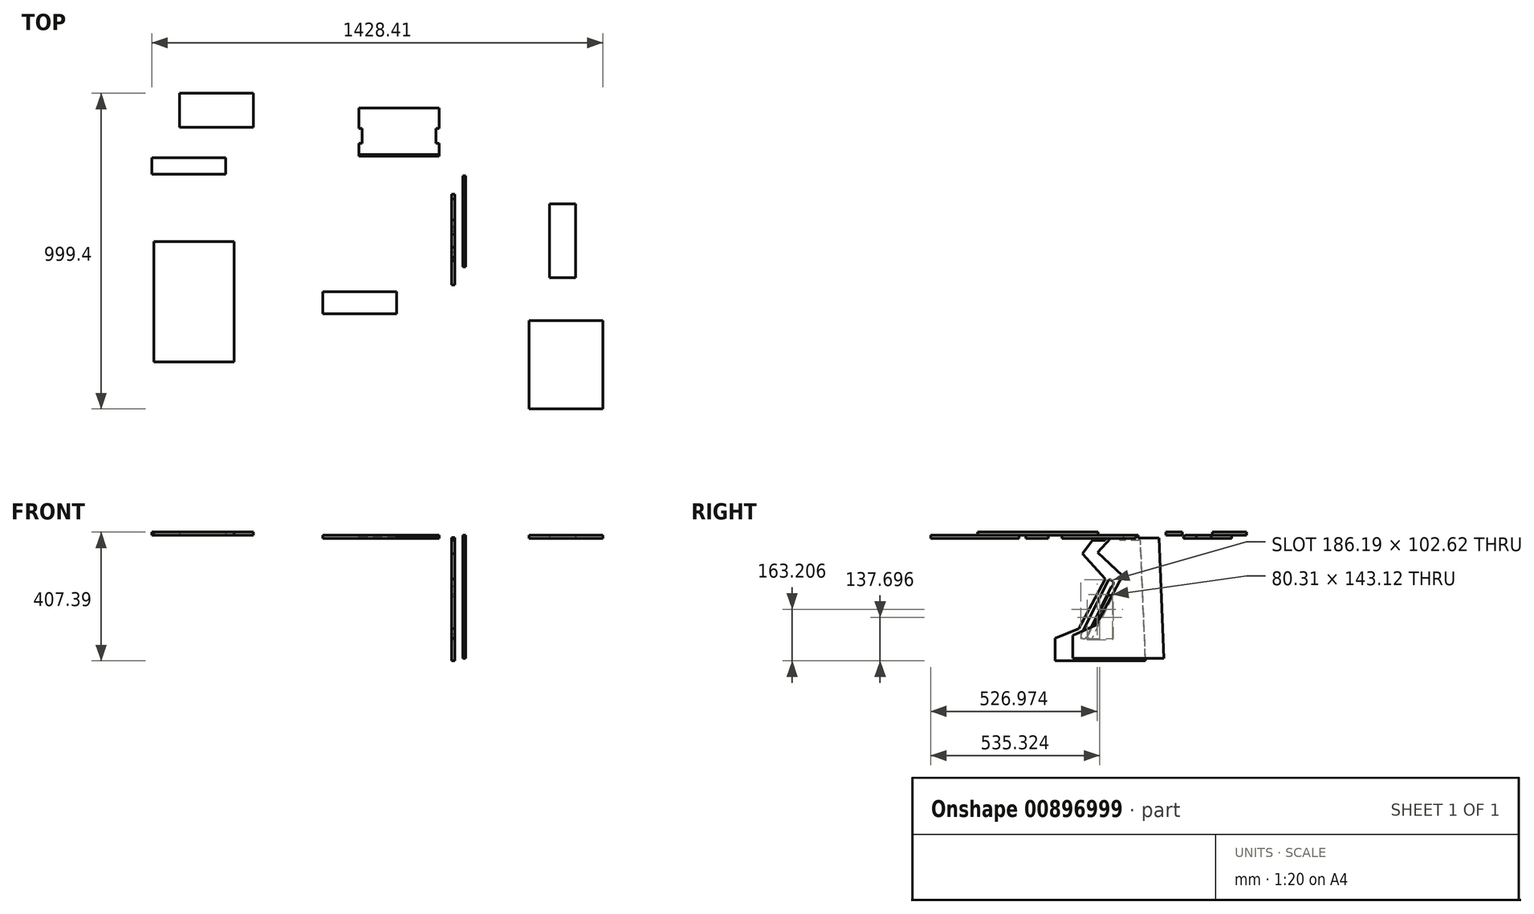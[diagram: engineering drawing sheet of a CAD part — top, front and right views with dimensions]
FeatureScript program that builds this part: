
annotation { "Feature Type Name" : "Feature", "Feature Type Description" : "" }
export const myFeature = defineFeature(function(context is Context, id is Id, definition is map)
    precondition{}
    {
        {
            var Q0;
            Q0=qCreatedBy(makeId("Right.planeOp"),FACE);
            var sketch = newSketch(context, id + "F0", { "sketchPlane" : qUnion([Q0])});
            skLineSegment(sketch, "E0", {"start": v(-57.5, -182.39) * mm, "end": v(221.9, -182.39) * mm});
            skLineSegment(sketch, "E1", {"start": v(221.9, -182.39) * mm, "end": v(205.76, 198.27) * mm});
            skLineSegment(sketch, "E2", {"start": v(94.6, 76.92) * mm, "end": v(10.95, -79.97) * mm});
            skLineSegment(sketch, "E3", {"start": v(-64.8, -182.39) * mm, "end": v(-57.5, -182.39) * mm});
            skLineSegment(sketch, "E4", {"start": v(94.6, 76.92) * mm, "end": v(21.95, 156.83) * mm});
            skLineSegment(sketch, "E5", {"start": v(21.95, 156.83) * mm, "end": v(53.36, 198.27) * mm});
            skLineSegment(sketch, "E6", {"start": v(10.95, -79.97) * mm, "end": v(-64.8, -111.39) * mm});
            skLineSegment(sketch, "E7", {"start": v(-64.8, -111.39) * mm, "end": v(-64.8, -182.39) * mm});
            skArc(sketch, "E8", {"start": v(112.88, 52.28) * mm, "mid": v(119.25, 66.78) * mm, "end": v(104.75, 73.15) * mm});
            skLineSegment(sketch, "E9", {"start": v(112.88, 52.28) * mm, "end": v(34.43, -107.28) * mm});
            skArc(sketch, "E10", {"start": v(18.86, -98.05) * mm, "mid": v(21.66, -111.08) * mm, "end": v(34.43, -107.28) * mm});
            skLineSegment(sketch, "E11", {"start": v(18.86, -98.05) * mm, "end": v(104.75, 73.15) * mm});
            skLineSegment(sketch, "E12", {"start": v(36.9, -108.73) * mm, "end": v(104.01, 26.86) * mm});
            skLineSegment(sketch, "E13", {"start": v(104.01, 26.86) * mm, "end": v(117.2, 20.33) * mm});
            skLineSegment(sketch, "E14", {"start": v(117.2, 20.33) * mm, "end": v(49.6, -116.25) * mm});
            skLineSegment(sketch, "E15", {"start": v(49.6, -116.25) * mm, "end": v(36.9, -108.73) * mm});
            skLineSegment(sketch, "E16", {"start": v(94.36, 198.27) * mm, "end": v(94.36, 207.6) * mm});
            skLineSegment(sketch, "E17", {"start": v(94.36, 207.6) * mm, "end": v(140.76, 207.6) * mm});
            skLineSegment(sketch, "E18", {"start": v(140.76, 207.6) * mm, "end": v(140.76, 198.27) * mm});
            skLineSegment(sketch, "E19", {"start": v(205.76, 198.27) * mm, "end": v(140.76, 198.27) * mm});
            skLineSegment(sketch, "E20", {"start": v(140.76, 198.27) * mm, "end": v(94.36, 198.27) * mm});
            skLineSegment(sketch, "E21", {"start": v(53.36, 198.27) * mm, "end": v(94.36, 198.27) * mm});
            skSolve(sketch);
        }
        {
            var Q0;
            Q0 = qSketchRegion(id + "F0", true);
            extrude(context, id + "F1", {"entities" : qUnion([Q0]), "depth" : 10 * mm, "offsetDistance" : 25 * mm});
        }
        {
            var Q0;
            Q0=makeQuery(id+"F1.opExtrude","CAP_FACE",FACE,{"disambiguationData":[OSD([sQuery(id+"F0.wireOp",EDGE,"E0"),sQuery(id+"F0.wireOp",EDGE,"E1"),sQuery(id+"F0.wireOp",EDGE,"lHdpLVMJ-1WkC-JgKl-GBrL-0Ag0FSk1Ueil"),sQuery(id+"F0.wireOp",EDGE,"8fRossxI-SsTZ-U6cr-KrP5-VSivJObJp7ZS"),sQuery(id+"F0.wireOp",EDGE,"kheAgBa6-kGJ1-7C4r-LUex-SDBD7PTxrj8S"),sQuery(id+"F0.wireOp",EDGE,"E2"),sQuery(id+"F0.wireOp",EDGE,"Q3xye6BH-dXEf-Nj2j-Apuc-TH6EefrlUt3x"),sQuery(id+"F0.wireOp",EDGE,"hmKdKFD2-3HO6-aGn5-Wh88-7PWj6mT0XpcJ"),sQuery(id+"F0.wireOp",EDGE,"E3")])],"isStart":true});
            cPlane(context, id + "F2", {"entities" : qUnion([Q0]), "cplaneType" : CPlaneType.OFFSET, "offset" : 0 * mm, "width" : 150 * mm, "height" : 150 * mm});
        }
        {
            var Q0;
            Q0=qCreatedBy(makeId("Top.planeOp"),FACE);
            cPlane(context, id + "F3", {"entities" : qUnion([Q0]), "cplaneType" : CPlaneType.OFFSET, "offset" : 205 * mm, "width" : 150 * mm, "height" : 150 * mm});
        }
        {
            var Q0;
            Q0=qCreatedBy(id+"F3.planeOp",FACE);
            var sketch = newSketch(context, id + "F4", { "sketchPlane" : qUnion([Q0])});
            skLineSegment(sketch, "E22.bottom", {"start": v(-293, 494.6) * mm, "end": v(-39, 494.6) * mm});
            skLineSegment(sketch, "E22.top", {"start": v(-293, 342.4) * mm, "end": v(-39.06, 342.4) * mm});
            skLineSegment(sketch, "E23", {"start": v(-293, 429.6) * mm, "end": v(-283, 429.6) * mm});
            skLineSegment(sketch, "E24", {"start": v(-283, 429.6) * mm, "end": v(-283, 383.4) * mm});
            skLineSegment(sketch, "E25", {"start": v(-283, 383.4) * mm, "end": v(-293, 383.4) * mm});
            skLineSegment(sketch, "E26", {"start": v(-293, 494.6) * mm, "end": v(-293, 429.6) * mm});
            skLineSegment(sketch, "E27", {"start": v(-293, 342.4) * mm, "end": v(-293, 383.4) * mm});
            skLineSegment(sketch, "E28", {"start": v(-39.06, 342.4) * mm, "end": v(-39.06, 383.4) * mm});
            skLineSegment(sketch, "E29", {"start": v(-39.06, 429.6) * mm, "end": v(-39, 494.6) * mm});
            skLineSegment(sketch, "E30", {"start": v(-39.06, 383.4) * mm, "end": v(-49.06, 383.4) * mm});
            skLineSegment(sketch, "E31", {"start": v(-49.06, 383.4) * mm, "end": v(-49.06, 429.6) * mm});
            skLineSegment(sketch, "E32", {"start": v(-49.06, 429.6) * mm, "end": v(-39.06, 429.6) * mm});
            skSolve(sketch);
        }
        {
            var Q0;
            Q0 = qSketchRegion(id + "F4", true);
            extrude(context, id + "F5", {"entities" : qUnion([Q0]), "depth" : 10 * mm, "offsetDistance" : 25 * mm});
        }
        {
            var Q0;
            Q0=makeQuery(id+"F5.opExtrude","CAP_FACE",FACE,{"disambiguationData":[OSD([sQuery(id+"F4.wireOp",EDGE,"E22.bottom"),sQuery(id+"F4.wireOp",EDGE,"E22.top"),sQuery(id+"F4.wireOp",EDGE,"E22.left"),sQuery(id+"F4.wireOp",EDGE,"E22.right")])],"isStart":false});
            cPlane(context, id + "F6", {"entities" : qUnion([Q0]), "cplaneType" : CPlaneType.OFFSET, "offset" : 0 * mm, "width" : 150 * mm, "height" : 150 * mm});
        }
        {
            var Q0;
            Q0=makeQuery(id+"F5.opExtrude","CAP_EDGE",EDGE,{"disambiguationData":[OSD([sQuery(id+"F4.wireOp",EDGE,"E22.top")])],"isStart":false});
            chamfer(context, id + "F7", {"entities" : qUnion([Q0]), "width" : 5 * mm, "tangentPropagation" : true});
        }
        {
            var Q0;
            Q0=makeQuery(id+"F1.opExtrude","CAP_FACE",FACE,{"disambiguationData":[OSD([sQuery(id+"F0.wireOp",EDGE,"E0"),sQuery(id+"F0.wireOp",EDGE,"E1"),sQuery(id+"F0.wireOp",EDGE,"lHdpLVMJ-1WkC-JgKl-GBrL-0Ag0FSk1Ueil"),sQuery(id+"F0.wireOp",EDGE,"8fRossxI-SsTZ-U6cr-KrP5-VSivJObJp7ZS"),sQuery(id+"F0.wireOp",EDGE,"kheAgBa6-kGJ1-7C4r-LUex-SDBD7PTxrj8S"),sQuery(id+"F0.wireOp",EDGE,"E2"),sQuery(id+"F0.wireOp",EDGE,"Q3xye6BH-dXEf-Nj2j-Apuc-TH6EefrlUt3x"),sQuery(id+"F0.wireOp",EDGE,"hmKdKFD2-3HO6-aGn5-Wh88-7PWj6mT0XpcJ"),sQuery(id+"F0.wireOp",EDGE,"E3")])],"isStart":false});
            cPlane(context, id + "F8", {"entities" : qUnion([Q0]), "cplaneType" : CPlaneType.OFFSET, "offset" : 25 * mm, "width" : 150 * mm, "height" : 150 * mm});
        }
        {
            var Q0;
            Q0=qCreatedBy(id+"F8.planeOp",FACE);
            var sketch = newSketch(context, id + "F9", { "sketchPlane" : qUnion([Q0])});
            skLineSegment(sketch, "E33", {"start": v(65.93, -69.22) * mm, "end": v(149.6, 87.67) * mm});
            skLineSegment(sketch, "E34", {"start": v(-7.92, -174.48) * mm, "end": v(0, -174.48) * mm});
            skLineSegment(sketch, "E35", {"start": v(0, -174.48) * mm, "end": v(279.4, -174.48) * mm});
            skLineSegment(sketch, "E36", {"start": v(279.4, -174.48) * mm, "end": v(264.18, 206.21) * mm});
            skLineSegment(sketch, "E37", {"start": v(149.6, 87.67) * mm, "end": v(70.54, 161.26) * mm});
            skLineSegment(sketch, "E38", {"start": v(70.54, 161.26) * mm, "end": v(111.78, 206.21) * mm});
            skLineSegment(sketch, "E39", {"start": v(65.93, -69.22) * mm, "end": v(-7.92, -102.48) * mm});
            skLineSegment(sketch, "E40", {"start": v(-7.92, -102.48) * mm, "end": v(-7.92, -174.48) * mm});
            skLineSegment(sketch, "E41", {"start": v(152.78, 206.21) * mm, "end": v(152.78, 215.53) * mm});
            skLineSegment(sketch, "E42", {"start": v(152.78, 215.53) * mm, "end": v(199.18, 215.53) * mm});
            skLineSegment(sketch, "E43", {"start": v(199.18, 215.53) * mm, "end": v(199.18, 206.21) * mm});
            skLineSegment(sketch, "E44", {"start": v(199.18, 206.21) * mm, "end": v(152.78, 206.21) * mm});
            skLineSegment(sketch, "E45", {"start": v(111.78, 206.21) * mm, "end": v(152.78, 206.21) * mm});
            skLineSegment(sketch, "E46", {"start": v(199.18, 206.21) * mm, "end": v(264.18, 206.21) * mm});
            skSolve(sketch);
        }
        {
            var Q0;
            Q0 = qSketchRegion(id + "F9", true);
            extrude(context, id + "F10", {"entities" : qUnion([Q0]), "depth" : 10 * mm, "offsetDistance" : 25 * mm});
        }
        {
            var Q0;
            Q0=qCreatedBy(id+"F6.planeOp",FACE);
            var sketch = newSketch(context, id + "F11", { "sketchPlane" : qUnion([Q0])});
            skLineSegment(sketch, "E47.bottom", {"start": v(-941.94, 71.6) * mm, "end": v(-687.94, 71.6) * mm});
            skLineSegment(sketch, "E47.top", {"start": v(-941.94, -309.4) * mm, "end": v(-687.94, -309.4) * mm});
            skLineSegment(sketch, "E47.left", {"start": v(-941.94, 71.6) * mm, "end": v(-941.94, -309.4) * mm});
            skLineSegment(sketch, "E47.right", {"start": v(-687.94, 71.6) * mm, "end": v(-687.94, -309.4) * mm});
            skSolve(sketch);
        }
        {
            var Q0;
            Q0 = qSketchRegion(id + "F11", true);
            extrude(context, id + "F12", {"entities" : qUnion([Q0]), "depth" : 10 * mm, "offsetDistance" : 25 * mm});
        }
        {
            var Q0;
            Q0=qCreatedBy(id+"F6.planeOp",FACE);
            var sketch = newSketch(context, id + "F13", { "sketchPlane" : qUnion([Q0])});
            skLineSegment(sketch, "E48.bottom", {"start": v(-949.25, 337.66) * mm, "end": v(-715.25, 337.66) * mm});
            skLineSegment(sketch, "E48.top", {"start": v(-949.25, 285.66) * mm, "end": v(-715.25, 285.66) * mm});
            skLineSegment(sketch, "E48.left", {"start": v(-949.25, 337.66) * mm, "end": v(-949.25, 285.66) * mm});
            skLineSegment(sketch, "E48.right", {"start": v(-715.25, 337.66) * mm, "end": v(-715.25, 285.66) * mm});
            skSolve(sketch);
        }
        {
            var Q0;
            Q0 = qSketchRegion(id + "F13", true);
            extrude(context, id + "F14", {"entities" : qUnion([Q0]), "depth" : 10 * mm, "offsetDistance" : 25 * mm});
        }
        {
            var Q0;
            Q0=qCreatedBy(id+"F6.planeOp",FACE);
            var sketch = newSketch(context, id + "F15", { "sketchPlane" : qUnion([Q0])});
            skLineSegment(sketch, "E49.bottom", {"start": v(-860.94, 541.13) * mm, "end": v(-626.94, 541.13) * mm});
            skLineSegment(sketch, "E49.top", {"start": v(-860.94, 433.13) * mm, "end": v(-626.94, 433.13) * mm});
            skLineSegment(sketch, "E49.left", {"start": v(-860.94, 541.13) * mm, "end": v(-860.94, 433.13) * mm});
            skLineSegment(sketch, "E49.right", {"start": v(-626.94, 541.13) * mm, "end": v(-626.94, 433.13) * mm});
            skSolve(sketch);
        }
        {
            var Q0;
            Q0 = qSketchRegion(id + "F15", true);
            extrude(context, id + "F16", {"entities" : qUnion([Q0]), "depth" : 10 * mm, "offsetDistance" : 25 * mm});
        }
        {
            var Q0;
            Q0=qCreatedBy(id+"F3.planeOp",FACE);
            var sketch = newSketch(context, id + "F17", { "sketchPlane" : qUnion([Q0])});
            skLineSegment(sketch, "E50.bottom", {"start": v(391.98, 191.52) * mm, "end": v(309.98, 191.52) * mm});
            skLineSegment(sketch, "E50.top", {"start": v(391.98, -42.48) * mm, "end": v(309.98, -42.48) * mm});
            skLineSegment(sketch, "E50.left", {"start": v(391.98, 191.52) * mm, "end": v(391.98, -42.48) * mm});
            skLineSegment(sketch, "E50.right", {"start": v(309.98, 191.52) * mm, "end": v(309.98, -42.48) * mm});
            skSolve(sketch);
        }
        {
            var Q0;
            Q0 = qSketchRegion(id + "F17", true);
            extrude(context, id + "F18", {"entities" : qUnion([Q0]), "depth" : 10 * mm, "offsetDistance" : 25 * mm});
        }
        {
            var Q0;
            Q0=qCreatedBy(id+"F3.planeOp",FACE);
            var sketch = newSketch(context, id + "F19", { "sketchPlane" : qUnion([Q0])});
            skLineSegment(sketch, "E51.bottom", {"start": v(-407.66, -86.47) * mm, "end": v(-173.66, -86.47) * mm});
            skLineSegment(sketch, "E51.top", {"start": v(-407.66, -157.47) * mm, "end": v(-173.66, -157.47) * mm});
            skLineSegment(sketch, "E51.left", {"start": v(-407.66, -86.47) * mm, "end": v(-407.66, -157.47) * mm});
            skLineSegment(sketch, "E51.right", {"start": v(-173.66, -86.47) * mm, "end": v(-173.66, -157.47) * mm});
            skSolve(sketch);
        }
        {
            var Q0;
            Q0 = qSketchRegion(id + "F19", true);
            extrude(context, id + "F20", {"entities" : qUnion([Q0]), "depth" : 10 * mm, "offsetDistance" : 25 * mm});
        }
        {
            var Q0;
            Q0=qCreatedBy(id+"F3.planeOp",FACE);
            var sketch = newSketch(context, id + "F21", { "sketchPlane" : qUnion([Q0])});
            skLineSegment(sketch, "E52.bottom", {"start": v(245.16, -178.87) * mm, "end": v(479.16, -178.87) * mm});
            skLineSegment(sketch, "E52.top", {"start": v(245.16, -458.27) * mm, "end": v(479.16, -458.27) * mm});
            skLineSegment(sketch, "E52.left", {"start": v(245.16, -178.87) * mm, "end": v(245.16, -458.27) * mm});
            skLineSegment(sketch, "E52.right", {"start": v(479.16, -178.87) * mm, "end": v(479.16, -458.27) * mm});
            skSolve(sketch);
        }
        {
            var Q0;
            Q0 = qSketchRegion(id + "F21", true);
            extrude(context, id + "F22", {"entities" : qUnion([Q0]), "depth" : 10 * mm, "offsetDistance" : 25 * mm});
        }
    });
